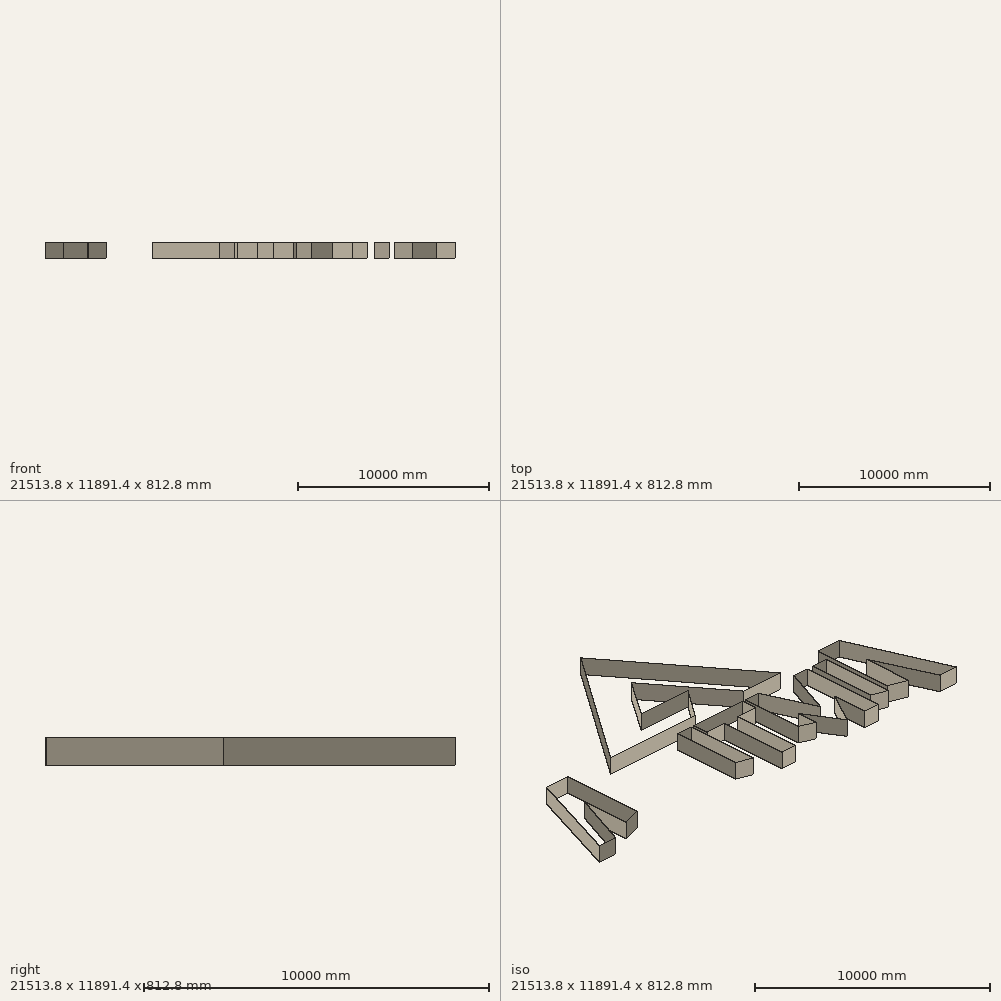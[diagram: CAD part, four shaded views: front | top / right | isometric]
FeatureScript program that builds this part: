
annotation { "Feature Type Name" : "Feature", "Feature Type Description" : "" }
export const myFeature = defineFeature(function(context is Context, id is Id, definition is map)
    precondition{}
    {
        {
            var Q0;
            Q0=qCreatedBy(makeId("Top.planeOp"),FACE);
            var sketch = newSketch(context, id + "F0", { "sketchPlane" : qUnion([Q0])});
            skLineSegment(sketch, "E0", {"start": v(-5118.12, -967.85) * mm, "end": v(-0.02, 5945.72) * mm});
            skLineSegment(sketch, "E1", {"start": v(-0.02, 5945.72) * mm, "end": v(5105.38, -967.85) * mm});
            skLineSegment(sketch, "E2", {"start": v(5105.38, -967.85) * mm, "end": v(2912.52, -967.85) * mm});
            skLineSegment(sketch, "E3", {"start": v(2912.52, -967.85) * mm, "end": v(25.38, 2929.47) * mm});
            skLineSegment(sketch, "E4", {"start": v(25.38, 2929.47) * mm, "end": v(-1568.47, 726.02) * mm});
            skLineSegment(sketch, "E5", {"start": v(-1568.47, 726.02) * mm, "end": v(1238.23, 726.02) * mm});
            skLineSegment(sketch, "E6", {"start": v(1238.23, 726.02) * mm, "end": v(-31.77, -967.85) * mm});
            skLineSegment(sketch, "E7", {"start": v(-31.77, -967.85) * mm, "end": v(-5118.12, -967.85) * mm});
            skLineSegment(sketch, "E8", {"start": v(-7552.28, -4997.44) * mm, "end": v(-7552.3, -827.65) * mm});
            skLineSegment(sketch, "E9", {"start": v(-7552.3, -827.65) * mm, "end": v(-8839.22, -827.65) * mm});
            skLineSegment(sketch, "E10", {"start": v(-8839.22, -827.65) * mm, "end": v(-10756.88, -5945.72) * mm});
            skLineSegment(sketch, "E11", {"start": v(-10756.88, -5945.72) * mm, "end": v(-9791.72, -5945.72) * mm});
            skLineSegment(sketch, "E12", {"start": v(-9791.72, -5945.72) * mm, "end": v(-8530.18, -2783.42) * mm});
            skLineSegment(sketch, "E13", {"start": v(-8530.18, -2783.42) * mm, "end": v(-8525.95, -5319.18) * mm});
            skLineSegment(sketch, "E14", {"start": v(-8525.95, -5319.18) * mm, "end": v(-7552.28, -4997.44) * mm});
            skLineSegment(sketch, "E15", {"start": v(-1651.02, -1534.6) * mm, "end": v(-829.75, -1534.6) * mm});
            skLineSegment(sketch, "E16", {"start": v(-829.75, -1534.6) * mm, "end": v(-829.75, -5289.54) * mm});
            skLineSegment(sketch, "E17", {"start": v(-829.75, -5289.54) * mm, "end": v(-1651.02, -5022.86) * mm});
            skLineSegment(sketch, "E18", {"start": v(-1651.02, -5022.86) * mm, "end": v(-1651.02, -1534.6) * mm});
            skLineSegment(sketch, "E19", {"start": v(-681.6, -1534.6) * mm, "end": v(2260.58, -1534.6) * mm});
            skLineSegment(sketch, "E20", {"start": v(2260.58, -1534.6) * mm, "end": v(2260.58, -2334.68) * mm});
            skLineSegment(sketch, "E21", {"start": v(2260.58, -2334.68) * mm, "end": v(1185.32, -2334.68) * mm});
            skLineSegment(sketch, "E22", {"start": v(1185.32, -2334.68) * mm, "end": v(1185.32, -5806.05) * mm});
            skLineSegment(sketch, "E23", {"start": v(1185.32, -5806.05) * mm, "end": v(376.76, -5806.05) * mm});
            skLineSegment(sketch, "E24", {"start": v(376.76, -5806.05) * mm, "end": v(376.76, -2334.68) * mm});
            skLineSegment(sketch, "E25", {"start": v(376.76, -2334.68) * mm, "end": v(-681.6, -2334.68) * mm});
            skLineSegment(sketch, "E26", {"start": v(-681.6, -2334.68) * mm, "end": v(-681.6, -1534.6) * mm});
            skLineSegment(sketch, "E27", {"start": v(2417.22, -1534.6) * mm, "end": v(3213.08, -1534.6) * mm});
            skLineSegment(sketch, "E28", {"start": v(3213.08, -1534.6) * mm, "end": v(4279.88, -4210.06) * mm});
            skLineSegment(sketch, "E29", {"start": v(4279.88, -4210.06) * mm, "end": v(5350.92, -1534.6) * mm});
            skLineSegment(sketch, "E30", {"start": v(5350.92, -1534.6) * mm, "end": v(6159.48, -1534.6) * mm});
            skLineSegment(sketch, "E31", {"start": v(6159.48, -1534.6) * mm, "end": v(6159.48, -5810.26) * mm});
            skLineSegment(sketch, "E32", {"start": v(6159.48, -5810.26) * mm, "end": v(5342.43, -5810.26) * mm});
            skLineSegment(sketch, "E33", {"start": v(5342.43, -5810.26) * mm, "end": v(5350.9, -3973) * mm});
            skLineSegment(sketch, "E34", {"start": v(5350.9, -3973) * mm, "end": v(4288.36, -5810.26) * mm});
            skLineSegment(sketch, "E35", {"start": v(4288.36, -5810.26) * mm, "end": v(3217.3, -3973) * mm});
            skLineSegment(sketch, "E36", {"start": v(3217.3, -3973) * mm, "end": v(3213.08, -5027.08) * mm});
            skLineSegment(sketch, "E37", {"start": v(3213.08, -5027.08) * mm, "end": v(2417.22, -4735) * mm});
            skLineSegment(sketch, "E38", {"start": v(2417.22, -4735) * mm, "end": v(2417.22, -1534.6) * mm});
            skLineSegment(sketch, "E39", {"start": v(6485.43, -1534.6) * mm, "end": v(7289.78, -1534.6) * mm});
            skLineSegment(sketch, "E40", {"start": v(7289.78, -1534.6) * mm, "end": v(7294, -5289.02) * mm});
            skLineSegment(sketch, "E41", {"start": v(7294, -5289.02) * mm, "end": v(6485.43, -5027.08) * mm});
            skLineSegment(sketch, "E42", {"start": v(6485.43, -5027.08) * mm, "end": v(6485.43, -1534.6) * mm});
            skLineSegment(sketch, "E43", {"start": v(7552.23, -797.97) * mm, "end": v(8832.68, -797.97) * mm});
            skLineSegment(sketch, "E44", {"start": v(8832.68, -797.97) * mm, "end": v(10756.88, -5920.3) * mm});
            skLineSegment(sketch, "E45", {"start": v(10756.88, -5920.3) * mm, "end": v(9782.15, -5920.3) * mm});
            skLineSegment(sketch, "E46", {"start": v(9782.15, -5920.3) * mm, "end": v(8521.68, -2753.78) * mm});
            skLineSegment(sketch, "E47", {"start": v(8521.68, -2753.78) * mm, "end": v(8517.43, -5289.02) * mm});
            skLineSegment(sketch, "E48", {"start": v(8517.43, -5289.02) * mm, "end": v(7552.23, -4963.58) * mm});
            skLineSegment(sketch, "E49", {"start": v(7552.23, -4963.58) * mm, "end": v(7552.23, -797.97) * mm});
            skSolve(sketch);
        }
        {
            var Q0;
            Q0=sQuery(id+"F0.wireOp",EDGE,"E42");
            var Q1;
            Q1=sQuery(id+"F0.wireOp",EDGE,"E26");
            var Q2;
            Q2=sQuery(id+"F0.wireOp",EDGE,"E19");
            var Q3;
            Q3=sQuery(id+"F0.wireOp",EDGE,"E35");
            var Q4;
            Q4=sQuery(id+"F0.wireOp",EDGE,"E13");
            var Q5;
            Q5=sQuery(id+"F0.wireOp",EDGE,"E14");
            var Q6;
            Q6=sQuery(id+"F0.wireOp",EDGE,"E15");
            var Q7;
            Q7=sQuery(id+"F0.wireOp",EDGE,"E0");
            var Q8;
            Q8=sQuery(id+"F0.wireOp",EDGE,"E1");
            var Q9;
            Q9=sQuery(id+"F0.wireOp",EDGE,"E2");
            var Q10;
            Q10=sQuery(id+"F0.wireOp",EDGE,"E3");
            var Q11;
            Q11=sQuery(id+"F0.wireOp",EDGE,"E4");
            var Q12;
            Q12=sQuery(id+"F0.wireOp",EDGE,"E5");
            var Q13;
            Q13=sQuery(id+"F0.wireOp",EDGE,"E6");
            var Q14;
            Q14=sQuery(id+"F0.wireOp",EDGE,"E7");
            var Q15;
            Q15=sQuery(id+"F0.wireOp",EDGE,"E8");
            var Q16;
            Q16=sQuery(id+"F0.wireOp",EDGE,"E9");
            var Q17;
            Q17=sQuery(id+"F0.wireOp",EDGE,"E10");
            var Q18;
            Q18=sQuery(id+"F0.wireOp",EDGE,"E11");
            var Q19;
            Q19=sQuery(id+"F0.wireOp",EDGE,"E34");
            var Q20;
            Q20=sQuery(id+"F0.wireOp",EDGE,"E12");
            var Q21;
            Q21=sQuery(id+"F0.wireOp",EDGE,"E43");
            var Q22;
            Q22=sQuery(id+"F0.wireOp",EDGE,"E27");
            var Q23;
            Q23=sQuery(id+"F0.wireOp",EDGE,"E39");
            var Q24;
            Q24=sQuery(id+"F0.wireOp",EDGE,"E23");
            var Q25;
            Q25=sQuery(id+"F0.wireOp",EDGE,"E20");
            var Q26;
            Q26=sQuery(id+"F0.wireOp",EDGE,"E29");
            var Q27;
            Q27=sQuery(id+"F0.wireOp",EDGE,"E36");
            var Q28;
            Q28=sQuery(id+"F0.wireOp",EDGE,"E16");
            var Q29;
            Q29=sQuery(id+"F0.wireOp",EDGE,"E48");
            var Q30;
            Q30=sQuery(id+"F0.wireOp",EDGE,"E32");
            var Q31;
            Q31=sQuery(id+"F0.wireOp",EDGE,"E44");
            var Q32;
            Q32=sQuery(id+"F0.wireOp",EDGE,"E28");
            var Q33;
            Q33=sQuery(id+"F0.wireOp",EDGE,"E40");
            var Q34;
            Q34=sQuery(id+"F0.wireOp",EDGE,"E24");
            var Q35;
            Q35=sQuery(id+"F0.wireOp",EDGE,"E21");
            var Q36;
            Q36=sQuery(id+"F0.wireOp",EDGE,"E46");
            var Q37;
            Q37=sQuery(id+"F0.wireOp",EDGE,"E30");
            var Q38;
            Q38=sQuery(id+"F0.wireOp",EDGE,"E17");
            var Q39;
            Q39=sQuery(id+"F0.wireOp",EDGE,"E49");
            var Q40;
            Q40=sQuery(id+"F0.wireOp",EDGE,"E33");
            var Q41;
            Q41=sQuery(id+"F0.wireOp",EDGE,"E41");
            var Q42;
            Q42=sQuery(id+"F0.wireOp",EDGE,"E25");
            var Q43;
            Q43=sQuery(id+"F0.wireOp",EDGE,"E22");
            var Q44;
            Q44=sQuery(id+"F0.wireOp",EDGE,"E47");
            var Q45;
            Q45=sQuery(id+"F0.wireOp",EDGE,"E31");
            var Q46;
            Q46=sQuery(id+"F0.wireOp",EDGE,"E38");
            var Q47;
            Q47=sQuery(id+"F0.wireOp",EDGE,"E18");
            var Q48;
            Q48=sQuery(id+"F0.wireOp",EDGE,"E37");
            var Q49;
            Q49=sQuery(id+"F0.wireOp",EDGE,"E45");
            extrude(context, id + "F1", {"bodyType" : ToolBodyType.SURFACE, "surfaceEntities" : qUnion([Q0, Q1, Q2, Q3, Q4, Q5, Q6, Q7, Q8, Q9, Q10, Q11, Q12, Q13, Q14, Q15, Q16, Q17, Q18, Q19, Q20, Q21, Q22, Q23, Q24, Q25, Q26, Q27, Q28, Q29, Q30, Q31, Q32, Q33, Q34, Q35, Q36, Q37, Q38, Q39, Q40, Q41, Q42, Q43, Q44, Q45, Q46, Q47, Q48, Q49]), "oppositeDirection" : true, "depth" : 812.8 * mm, "offsetDistance" : 25.4 * mm});
        }
    });
